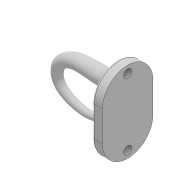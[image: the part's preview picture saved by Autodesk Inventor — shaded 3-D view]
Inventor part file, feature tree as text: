
AUTODESK INVENTOR PART (.ipt)
format: ipt  version: 2018 (Build 220112000, 112)  size: 283,136 bytes
history: native  units: mm
features: sketch x5, plane x1, sweep x1, extrude x1, hole x1, fillet x1
ambient origin geometry x8: Origin, YZ Plane, XZ Plane, XY Plane, X Axis, Y Axis, Z Axis, Center Point
bodies: Solid1 (feature_tree)
feature tree (10):
  sketch  "Sketch1"  dims[d3=8.0mm d5=16.0mm]
  sketch  "Sketch2"  dims[d6=8.0mm d7=40.0mm]
  plane  "Work Plane3"
  sketch  "Sketch4"  dims[d9=3.0mm d10=-0.390954mm d11=0.0mm d15=25.0mm]
  sweep  "Sweep1"
  extrude  "Extrusion1"  Depth=40.0mm
  hole  "Hole1"  [1 undecoded]
  fillet  "Fillet1"  Radius=25.0mm
  sketch  "Sketch5"  dims[d16=25.0mm]
  sketch  "Sketch7"  dims[d17=15.0mm d21=5.0mm d22=0.0mm d25=6.25mm d26=6.25mm d27=7.5mm d28=4.0mm d29=4.369mm d30=5.0mm d31=2.0mm d32=90.0deg d33=8.0mm d34=20.594885mm d35=1.0mm d36=8.96mm]
note: 1 required parameter value undecoded (feature->parameter linkage not recoverable at this tier; creation-order binding heuristic only, values carry confidence <= 0.55)
